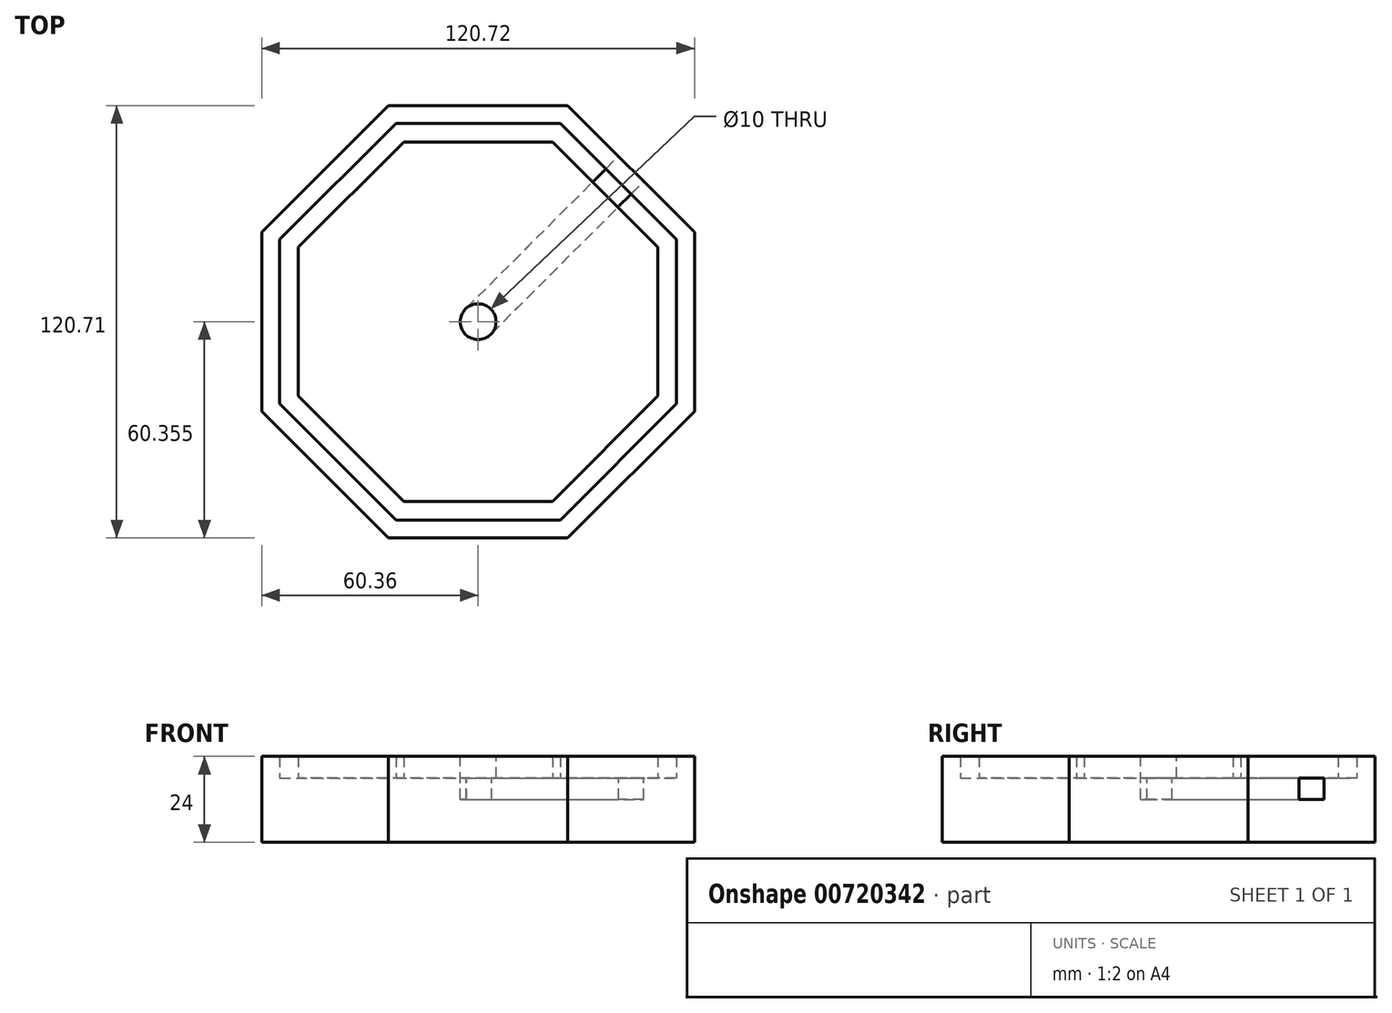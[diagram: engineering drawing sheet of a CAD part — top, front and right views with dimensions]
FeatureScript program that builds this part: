
annotation { "Feature Type Name" : "Feature", "Feature Type Description" : "" }
export const myFeature = defineFeature(function(context is Context, id is Id, definition is map)
    precondition{}
    {
        {
            var Q0;
            Q0=qCreatedBy(makeId("Top.planeOp"),FACE);
            var sketch = newSketch(context, id + "F0", { "sketchPlane" : qUnion([Q0])});
            skLineSegment(sketch, "E0", {"start": v(0, 0) * mm, "end": v(50, 0) * mm});
            skLineSegment(sketch, "E1", {"start": v(50, 0) * mm, "end": v(85.36, 35.36) * mm});
            skLineSegment(sketch, "E2", {"start": v(85.36, 35.36) * mm, "end": v(85.36, 85.36) * mm});
            skLineSegment(sketch, "E3", {"start": v(85.36, 85.36) * mm, "end": v(50, 120.71) * mm});
            skLineSegment(sketch, "E4", {"start": v(50, 120.71) * mm, "end": v(0, 120.71) * mm});
            skLineSegment(sketch, "E5", {"start": v(0, 120.71) * mm, "end": v(-35.36, 85.36) * mm});
            skLineSegment(sketch, "E6", {"start": v(-35.36, 85.36) * mm, "end": v(-35.36, 35.36) * mm});
            skLineSegment(sketch, "E7", {"start": v(-35.36, 35.36) * mm, "end": v(0, 0) * mm});
            skLineSegment(sketch, "E8", {"start": v(25, 120.71) * mm, "end": v(25, 0) * mm});
            skSolve(sketch);
        }
        {
            var Q0;
            Q0=makeQuery(id+"F0.imprint","IMPRINT",FACE,{"disambiguationData":[TD([[makeQuery(id+"F0.imprint","IMPRINT",EDGE,{"derivedFrom":sQuery(id+"F0.wireOp",EDGE,"E0")}),1.0]])]});
            extrude(context, id + "F1", {"entities" : qUnion([Q0]), "depth" : 18 * mm, "offsetDistance" : 25 * mm});
        }
        {
            var Q0;
            Q0=makeQuery(id+"F1.opExtrude","CAP_FACE",FACE,{"disambiguationData":[OSD([sQuery(id+"F0.wireOp",EDGE,"E0"),sQuery(id+"F0.wireOp",EDGE,"E1"),sQuery(id+"F0.wireOp",EDGE,"E2"),sQuery(id+"F0.wireOp",EDGE,"E3"),sQuery(id+"F0.wireOp",EDGE,"E4"),sQuery(id+"F0.wireOp",EDGE,"E5"),sQuery(id+"F0.wireOp",EDGE,"E6"),sQuery(id+"F0.wireOp",EDGE,"E7")])],"isStart":false});
            var sketch = newSketch(context, id + "F2", { "sketchPlane" : qUnion([Q0])});
            skLineSegment(sketch, "E9", {"start": v(-35.36, 35.36) * mm, "end": v(-35.36, 85.36) * mm});
            skLineSegment(sketch, "E10", {"start": v(-35.36, 85.36) * mm, "end": v(0, 120.71) * mm});
            skLineSegment(sketch, "E11", {"start": v(0, 120.71) * mm, "end": v(50, 120.71) * mm});
            skLineSegment(sketch, "E12", {"start": v(50, 120.71) * mm, "end": v(85.36, 85.36) * mm});
            skLineSegment(sketch, "E13", {"start": v(85.36, 85.36) * mm, "end": v(85.36, 35.36) * mm});
            skLineSegment(sketch, "E14", {"start": v(85.36, 35.36) * mm, "end": v(50, 0) * mm});
            skLineSegment(sketch, "E15", {"start": v(50, 0) * mm, "end": v(0, 0) * mm});
            skLineSegment(sketch, "E16", {"start": v(0, 0) * mm, "end": v(-35.36, 35.36) * mm});
            skLineSegment(sketch, "E17.0", {"start": v(-30.36, 37.43) * mm, "end": v(-30.36, 83.28) * mm});
            skLineSegment(sketch, "E17.1", {"start": v(2.07, 5) * mm, "end": v(-30.36, 37.43) * mm});
            skLineSegment(sketch, "E17.2", {"start": v(-30.36, 83.28) * mm, "end": v(2.07, 115.71) * mm});
            skLineSegment(sketch, "E17.3", {"start": v(47.93, 5) * mm, "end": v(2.07, 5) * mm});
            skLineSegment(sketch, "E17.4", {"start": v(2.07, 115.71) * mm, "end": v(47.93, 115.71) * mm});
            skLineSegment(sketch, "E17.5", {"start": v(47.93, 115.71) * mm, "end": v(80.36, 83.28) * mm});
            skLineSegment(sketch, "E17.6", {"start": v(80.36, 83.28) * mm, "end": v(80.36, 37.43) * mm});
            skLineSegment(sketch, "E17.7", {"start": v(80.36, 37.43) * mm, "end": v(47.93, 5) * mm});
            skLineSegment(sketch, "E18.0", {"start": v(-25.16, 39.58) * mm, "end": v(-25.16, 81.13) * mm});
            skLineSegment(sketch, "E18.1", {"start": v(4.22, 10.2) * mm, "end": v(-25.16, 39.58) * mm});
            skLineSegment(sketch, "E18.2", {"start": v(-25.16, 81.13) * mm, "end": v(4.22, 110.51) * mm});
            skLineSegment(sketch, "E18.3", {"start": v(45.78, 10.2) * mm, "end": v(4.22, 10.2) * mm});
            skLineSegment(sketch, "E18.4", {"start": v(4.22, 110.51) * mm, "end": v(45.78, 110.51) * mm});
            skLineSegment(sketch, "E18.5", {"start": v(45.78, 110.51) * mm, "end": v(75.16, 81.13) * mm});
            skLineSegment(sketch, "E18.6", {"start": v(75.16, 81.13) * mm, "end": v(75.16, 39.58) * mm});
            skLineSegment(sketch, "E18.7", {"start": v(75.16, 39.58) * mm, "end": v(45.78, 10.2) * mm});
            skSolve(sketch);
        }
        {
            var Q0;
            Q0=makeQuery(id+"F2.imprint","IMPRINT",FACE,{"disambiguationData":[TD([[makeQuery(id+"F2.imprint","IMPRINT",EDGE,{"derivedFrom":sQuery(id+"F2.wireOp",EDGE,"E9")}),1.0]])]});
            var Q1;
            Q1=makeQuery(id+"F2.imprint","IMPRINT",FACE,{"disambiguationData":[TD([[makeQuery(id+"F2.imprint","IMPRINT",EDGE,{"derivedFrom":sQuery(id+"F2.wireOp",EDGE,"E18.0")}),-1.0]])]});
            extrude(context, id + "F3", {"entities" : qUnion([Q0, Q1]), "operationType" : NewBodyOperationType.ADD, "depth" : 6 * mm, "offsetDistance" : 25 * mm});
        }
        {
            var Q0;
            Q0=makeQuery(id+"F3.opExtrude","CAP_FACE",FACE,{"disambiguationData":[OSD([sQuery(id+"F2.wireOp",EDGE,"E18.0"),sQuery(id+"F2.wireOp",EDGE,"E18.1"),sQuery(id+"F2.wireOp",EDGE,"E18.2"),sQuery(id+"F2.wireOp",EDGE,"E18.3"),sQuery(id+"F2.wireOp",EDGE,"E18.4"),sQuery(id+"F2.wireOp",EDGE,"E18.5"),sQuery(id+"F2.wireOp",EDGE,"E18.6"),sQuery(id+"F2.wireOp",EDGE,"E18.7")])],"isStart":false});
            var sketch = newSketch(context, id + "F4", { "sketchPlane" : qUnion([Q0])});
            skCircle(sketch, "E19", {"center": v(25, 60.36) * mm, "radius": 5 * mm});
            skSolve(sketch);
        }
        {
            var Q0;
            Q0=makeQuery(id+"F4.imprint","IMPRINT",FACE,{"disambiguationData":[TD([[makeQuery(id+"F4.imprint","IMPRINT",EDGE,{"derivedFrom":sQuery(id+"F4.wireOp",EDGE,"E19")}),1.0]])]});
            extrude(context, id + "F5", {"entities" : qUnion([Q0]), "operationType" : NewBodyOperationType.REMOVE, "oppositeDirection" : true, "depth" : 12 * mm, "offsetDistance" : 25 * mm});
        }
        {
            var Q0;
            Q0=makeQuery(id+"F3.boolean.opBoolean","MERGE",FACE,{"derivedFrom":[makeQuery(id+"F1.opExtrude","SWEPT_FACE",FACE,{"disambiguationData":[OSD([sQuery(id+"F0.wireOp",EDGE,"E3")])]}),makeQuery(id+"F3.opExtrude","SWEPT_FACE",FACE,{"disambiguationData":[OSD([sQuery(id+"F2.wireOp",EDGE,"E12")])]})]});
            var sketch = newSketch(context, id + "F6", { "sketchPlane" : qUnion([Q0])});
            skLineSegment(sketch, "E20", {"start": v(20, 12) * mm, "end": v(20, 18) * mm});
            skLineSegment(sketch, "E21", {"start": v(20, 18) * mm, "end": v(30, 18) * mm});
            skLineSegment(sketch, "E22", {"start": v(20, 12) * mm, "end": v(30, 12) * mm});
            skLineSegment(sketch, "E23", {"start": v(30, 12) * mm, "end": v(30, 18) * mm});
            skSolve(sketch);
        }
        {
            var Q0;
            Q0=makeQuery(id+"F6.imprint","IMPRINT",FACE,{"disambiguationData":[TD([[makeQuery(id+"F6.imprint","IMPRINT",EDGE,{"derivedFrom":sQuery(id+"F6.wireOp",EDGE,"E20")}),-1.0]])]});
            extrude(context, id + "F7", {"entities" : qUnion([Q0]), "operationType" : NewBodyOperationType.REMOVE, "oppositeDirection" : true, "depth" : 60 * mm, "offsetDistance" : 25 * mm});
        }
    });
